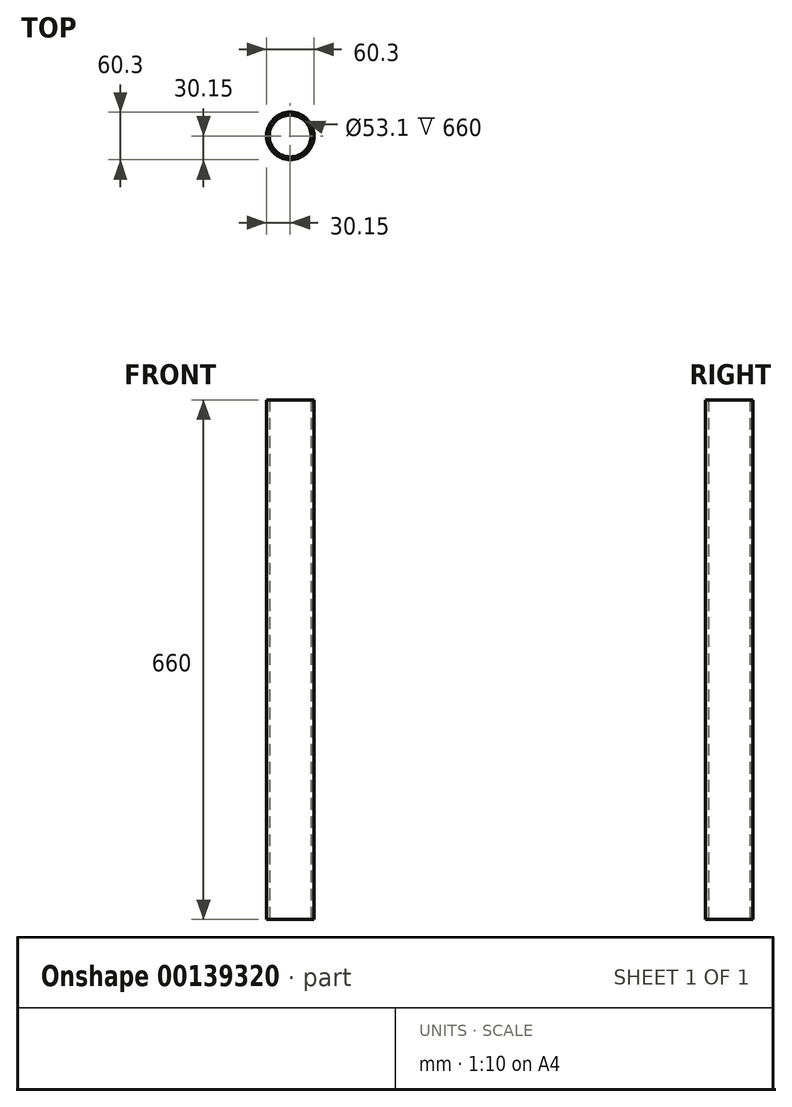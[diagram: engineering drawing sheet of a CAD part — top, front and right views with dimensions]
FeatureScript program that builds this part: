
annotation { "Feature Type Name" : "Feature", "Feature Type Description" : "" }
export const myFeature = defineFeature(function(context is Context, id is Id, definition is map)
    precondition{}
    {
        {
            var Q0;
            Q0=qCreatedBy(makeId("Top.planeOp"),FACE);
            var sketch = newSketch(context, id + "F0", { "sketchPlane" : qUnion([Q0])});
            skCircle(sketch, "E0", {"center": v(0, 0) * mm, "radius": 30.15 * mm});
            skCircle(sketch, "E1", {"center": v(0, 0) * mm, "radius": 26.55 * mm});
            skSolve(sketch);
        }
        {
            var Q0;
            Q0 = qSketchRegion(id + "F0", true);
            extrude(context, id + "F1", {"entities" : qUnion([Q0]), "depth" : 660 * mm});
        }
    });
